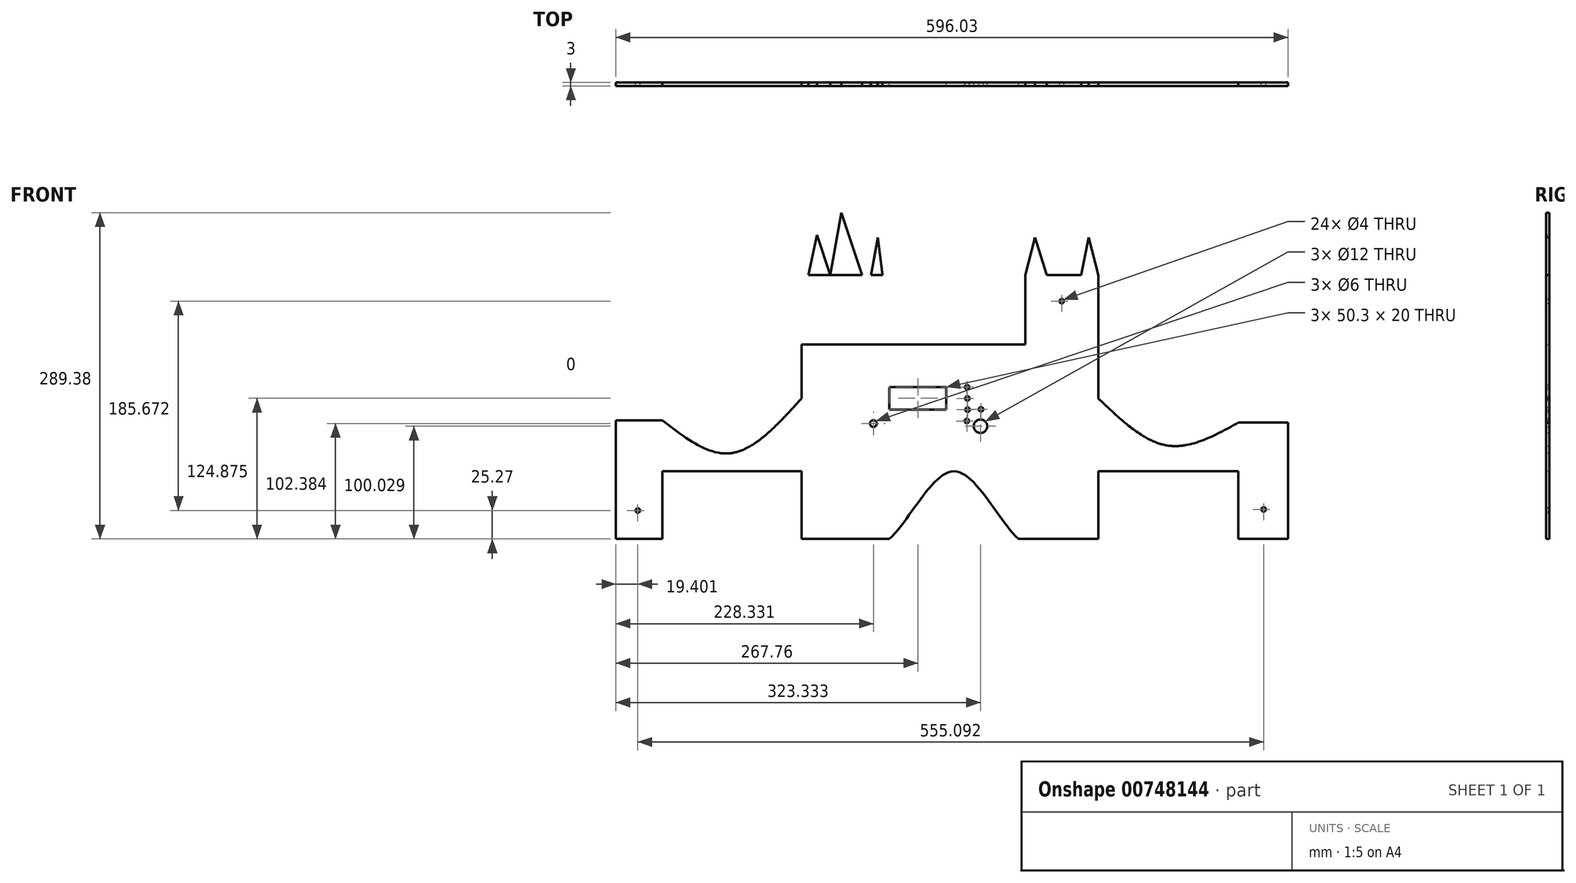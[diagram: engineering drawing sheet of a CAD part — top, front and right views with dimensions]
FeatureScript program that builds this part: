
annotation { "Feature Type Name" : "Feature", "Feature Type Description" : "" }
export const myFeature = defineFeature(function(context is Context, id is Id, definition is map)
    precondition{}
    {
        {
            var Q0;
            Q0=qCreatedBy(makeId("Front.planeOp"),FACE);
            var sketch = newSketch(context, id + "F0", { "sketchPlane" : qUnion([Q0])});
            skLineSegment(sketch, "E0", {"start": v(-242.6, -122.29) * mm, "end": v(-242.6, -42.29) * mm});
            skLineSegment(sketch, "E1", {"start": v(-242.6, -42.29) * mm, "end": v(-201.52, -42.29) * mm});
            skLineSegment(sketch, "E2", {"start": v(-201.52, -42.29) * mm, "end": v(-201.52, -87.66) * mm});
            skLineSegment(sketch, "E3", {"start": v(-201.52, -87.66) * mm, "end": v(-241.16, -87.66) * mm});
            skLineSegment(sketch, "E4", {"start": v(-201.52, -87.66) * mm, "end": v(-78.03, -87.66) * mm});
            skLineSegment(sketch, "E5", {"start": v(-242.6, -122.29) * mm, "end": v(-242.6, -147.66) * mm});
            skLineSegment(sketch, "E6", {"start": v(-242.6, -147.66) * mm, "end": v(-201.52, -147.66) * mm});
            skLineSegment(sketch, "E7", {"start": v(-201.52, -147.66) * mm, "end": v(-201.52, -87.66) * mm});
            skLineSegment(sketch, "E8", {"start": v(-78.03, -87.66) * mm, "end": v(-78.03, -147.66) * mm});
            skLineSegment(sketch, "E9", {"start": v(-78.03, -147.66) * mm, "end": v(0, -147.66) * mm});
            skLineSegment(sketch, "E10", {"start": v(-78.03, -87.66) * mm, "end": v(0, -87.66) * mm});
            skLineSegment(sketch, "E11", {"start": v(0, -87.66) * mm, "end": v(0, -147.66) * mm});
            skLineSegment(sketch, "E12", {"start": v(-78.03, -87.66) * mm, "end": v(-78.03, 24.85) * mm});
            skLineSegment(sketch, "E13", {"start": v(-78.03, 24.85) * mm, "end": v(0, 24.85) * mm});
            skLineSegment(sketch, "E14", {"start": v(0, 24.85) * mm, "end": v(0, -87.66) * mm});
            skLineSegment(sketch, "E15", {"start": v(0, -87.66) * mm, "end": v(114.45, -87.66) * mm});
            skLineSegment(sketch, "E16", {"start": v(117.61, -147.66) * mm, "end": v(185.23, -147.66) * mm});
            skLineSegment(sketch, "E17", {"start": v(185.23, -147.66) * mm, "end": v(185.23, -87.66) * mm});
            skLineSegment(sketch, "E18", {"start": v(185.23, -87.66) * mm, "end": v(114.45, -87.66) * mm});
            skLineSegment(sketch, "E19", {"start": v(114.45, -87.66) * mm, "end": v(114.45, -147.66) * mm});
            skLineSegment(sketch, "E20", {"start": v(114.45, -147.66) * mm, "end": v(117.61, -147.66) * mm});
            skLineSegment(sketch, "E21", {"start": v(114.45, -87.66) * mm, "end": v(114.45, 24.85) * mm});
            skLineSegment(sketch, "E22", {"start": v(185.23, -87.66) * mm, "end": v(185.23, 24.85) * mm});
            skLineSegment(sketch, "E23", {"start": v(185.23, 24.85) * mm, "end": v(114.45, 24.85) * mm});
            skLineSegment(sketch, "E24", {"start": v(-71.9, 24.85) * mm, "end": v(-71.9, 86.5) * mm});
            skLineSegment(sketch, "E25", {"start": v(-6.12, 24.85) * mm, "end": v(-6.12, 86.5) * mm});
            skLineSegment(sketch, "E26", {"start": v(-6.12, 86.5) * mm, "end": v(-6.12, 24.85) * mm});
            skLineSegment(sketch, "E27", {"start": v(-6.12, 86.5) * mm, "end": v(-71.9, 86.5) * mm});
            skLineSegment(sketch, "E28", {"start": v(0, 24.85) * mm, "end": v(114.45, 24.85) * mm});
            skLineSegment(sketch, "E29", {"start": v(0, 13.97) * mm, "end": v(114.45, 13.97) * mm});
            skLineSegment(sketch, "E30", {"start": v(114.45, 13.97) * mm, "end": v(93.44, 24.85) * mm});
            skLineSegment(sketch, "E31", {"start": v(93.44, 24.85) * mm, "end": v(80.38, 13.97) * mm});
            skLineSegment(sketch, "E32", {"start": v(80.38, 13.97) * mm, "end": v(71.32, 24.85) * mm});
            skLineSegment(sketch, "E33", {"start": v(71.32, 24.85) * mm, "end": v(58.25, 13.97) * mm});
            skLineSegment(sketch, "E34", {"start": v(58.25, 13.97) * mm, "end": v(49.19, 24.85) * mm});
            skLineSegment(sketch, "E35", {"start": v(49.19, 24.85) * mm, "end": v(36.12, 13.97) * mm});
            skLineSegment(sketch, "E36", {"start": v(36.12, 13.97) * mm, "end": v(27.06, 24.85) * mm});
            skLineSegment(sketch, "E37", {"start": v(27.06, 24.85) * mm, "end": v(14, 13.97) * mm});
            skLineSegment(sketch, "E38", {"start": v(14, 13.97) * mm, "end": v(0, 24.85) * mm});
            skLineSegment(sketch, "E39", {"start": v(120.47, 24.85) * mm, "end": v(120.47, 86.5) * mm});
            skLineSegment(sketch, "E40", {"start": v(185.23, 24.85) * mm, "end": v(185.23, 86.5) * mm});
            skLineSegment(sketch, "E41", {"start": v(185.23, 86.5) * mm, "end": v(120.47, 86.5) * mm});
            skFitSpline(sketch, "E42", {"points": [v(0, -147.66) * mm, v(57.23, -87.66) * mm, v(114.45, -147.66) * mm], "startDerivative": vector(114.45, 108.74) * mm, "endDerivative": vector(114.45, -108.74) * mm});
            skLineSegment(sketch, "E43", {"start": v(-71.9, 86.5) * mm, "end": v(-64.41, 121.91) * mm});
            skLineSegment(sketch, "E44", {"start": v(-64.41, 121.91) * mm, "end": v(-52.56, 86.5) * mm});
            skLineSegment(sketch, "E45", {"start": v(-52.56, 86.5) * mm, "end": v(-42.84, 141.72) * mm});
            skLineSegment(sketch, "E46", {"start": v(-42.84, 141.72) * mm, "end": v(-24.36, 86.5) * mm});
            skLineSegment(sketch, "E47", {"start": v(-16.37, 86.5) * mm, "end": v(-10.42, 119.89) * mm});
            skLineSegment(sketch, "E48", {"start": v(-10.42, 119.89) * mm, "end": v(-6.12, 86.5) * mm});
            skLineSegment(sketch, "E49", {"start": v(120.47, 86.5) * mm, "end": v(129.04, 119.89) * mm});
            skLineSegment(sketch, "E50", {"start": v(129.04, 119.89) * mm, "end": v(139.65, 86.5) * mm});
            skLineSegment(sketch, "E51", {"start": v(139.65, 86.5) * mm, "end": v(152.85, 86.5) * mm});
            skLineSegment(sketch, "E52", {"start": v(139.65, 86.5) * mm, "end": v(149.07, 132.75) * mm});
            skLineSegment(sketch, "E53", {"start": v(149.07, 132.75) * mm, "end": v(163.78, 86.5) * mm});
            skLineSegment(sketch, "E54", {"start": v(163.78, 86.5) * mm, "end": v(169.95, 86.5) * mm});
            skLineSegment(sketch, "E55", {"start": v(169.95, 86.5) * mm, "end": v(176.75, 119.89) * mm});
            skLineSegment(sketch, "E56", {"start": v(176.75, 119.89) * mm, "end": v(185.23, 86.5) * mm});
            skLineSegment(sketch, "E57", {"start": v(185.23, -87.66) * mm, "end": v(309.46, -87.66) * mm});
            skLineSegment(sketch, "E58", {"start": v(309.46, -87.66) * mm, "end": v(353.42, -87.66) * mm});
            skLineSegment(sketch, "E59", {"start": v(353.42, -87.66) * mm, "end": v(353.42, -147.66) * mm});
            skLineSegment(sketch, "E60", {"start": v(353.42, -147.66) * mm, "end": v(309.46, -147.66) * mm});
            skLineSegment(sketch, "E61", {"start": v(309.46, -147.66) * mm, "end": v(309.46, -87.66) * mm});
            skLineSegment(sketch, "E62", {"start": v(309.46, -87.66) * mm, "end": v(309.46, -44.44) * mm});
            skLineSegment(sketch, "E63", {"start": v(309.46, -44.44) * mm, "end": v(353.42, -44.44) * mm});
            skLineSegment(sketch, "E64", {"start": v(353.42, -44.44) * mm, "end": v(353.42, -87.66) * mm});
            skPoint(sketch, "E65.1.internal.snap0", {"position": v(247.35, -87.66) * mm});
            skFitSpline(sketch, "E65", {"points": [v(309.46, -44.44) * mm, v(247.35, -64.83) * mm, v(185.23, -22.93) * mm], "startDerivative": vector(-130.66, -71.98) * mm, "endDerivative": vector(-117.95, 112.9) * mm});
            skFitSpline(sketch, "E66", {"points": [v(-201.52, -42.29) * mm, v(-141.53, -71.6) * mm, v(-78.03, -22.93) * mm], "startDerivative": vector(126.66, -98.3) * mm, "endDerivative": vector(120.42, 133.53) * mm});
            skPoint(sketch, "E67.2.internal.snap0", {"position": v(-222.06, -42.29) * mm});
            skFitSpline(sketch, "E67", {"points": [v(-201.52, -58.4) * mm, v(-141.53, -81.5) * mm, v(-78.03, -42.29) * mm], "startDerivative": vector(125.17, -77.74) * mm, "endDerivative": vector(121.86, 107.67) * mm});
            skFitSpline(sketch, "E68", {"points": [v(309.46, -58.4) * mm, v(247.35, -78.2) * mm, v(185.23, -42.29) * mm], "startDerivative": vector(-128.74, -67.59) * mm, "endDerivative": vector(-119.8, 98.5) * mm});
            skLineSegment(sketch, "E69", {"start": v(-201.52, -42.29) * mm, "end": v(-191.14, -64.78) * mm});
            skLineSegment(sketch, "E70", {"start": v(-191.14, -64.78) * mm, "end": v(-181.36, -57.93) * mm});
            skLineSegment(sketch, "E71", {"start": v(-181.36, -57.93) * mm, "end": v(-168.22, -76.69) * mm});
            skLineSegment(sketch, "E72", {"start": v(-168.22, -76.69) * mm, "end": v(-159.93, -70.88) * mm});
            skLineSegment(sketch, "E73", {"start": v(-159.93, -70.88) * mm, "end": v(-147.57, -81.64) * mm});
            skLineSegment(sketch, "E74", {"start": v(-147.57, -81.64) * mm, "end": v(-141.53, -71.6) * mm});
            skLineSegment(sketch, "E75", {"start": v(-141.53, -71.6) * mm, "end": v(-129.63, -78.78) * mm});
            skLineSegment(sketch, "E76", {"start": v(-129.63, -78.78) * mm, "end": v(-120.3, -63.3) * mm});
            skLineSegment(sketch, "E77", {"start": v(-120.3, -63.3) * mm, "end": v(-106.51, -71.6) * mm});
            skLineSegment(sketch, "E78", {"start": v(-106.51, -71.6) * mm, "end": v(-106.51, -52.51) * mm});
            skLineSegment(sketch, "E79", {"start": v(-106.51, -52.51) * mm, "end": v(-89.72, -52.51) * mm});
            skLineSegment(sketch, "E80", {"start": v(-89.72, -52.51) * mm, "end": v(-89.72, -35.76) * mm});
            skLineSegment(sketch, "E81", {"start": v(-89.72, -35.76) * mm, "end": v(-78.03, -42.29) * mm});
            skLineSegment(sketch, "E82", {"start": v(309.46, -44.44) * mm, "end": v(297.99, -64.35) * mm});
            skLineSegment(sketch, "E83", {"start": v(297.99, -64.35) * mm, "end": v(288.43, -56.03) * mm});
            skLineSegment(sketch, "E84", {"start": v(288.43, -56.03) * mm, "end": v(276.13, -73.97) * mm});
            skLineSegment(sketch, "E85", {"start": v(276.13, -73.97) * mm, "end": v(262.39, -64.47) * mm});
            skLineSegment(sketch, "E86", {"start": v(262.39, -64.47) * mm, "end": v(255.13, -78.43) * mm});
            skLineSegment(sketch, "E87", {"start": v(255.13, -78.43) * mm, "end": v(247.35, -64.83) * mm});
            skLineSegment(sketch, "E88", {"start": v(234.7, -75.2) * mm, "end": v(247.35, -64.83) * mm});
            skLineSegment(sketch, "E89", {"start": v(234.7, -75.2) * mm, "end": v(224.65, -56.03) * mm});
            skLineSegment(sketch, "E90", {"start": v(224.65, -56.03) * mm, "end": v(214.66, -64.83) * mm});
            skLineSegment(sketch, "E91", {"start": v(214.66, -64.83) * mm, "end": v(214.66, -52.51) * mm});
            skLineSegment(sketch, "E92", {"start": v(214.66, -52.51) * mm, "end": v(205.67, -59.1) * mm});
            skLineSegment(sketch, "E93", {"start": v(205.56, -42.39) * mm, "end": v(205.67, -59.1) * mm});
            skLineSegment(sketch, "E94", {"start": v(205.56, -42.39) * mm, "end": v(192.73, -48.43) * mm});
            skLineSegment(sketch, "E95", {"start": v(192.73, -48.43) * mm, "end": v(192.73, -30.08) * mm});
            skLineSegment(sketch, "E96", {"start": v(185.23, -42.29) * mm, "end": v(192.73, -30.08) * mm});
            skLineSegment(sketch, "E97", {"start": v(-191.14, -64.78) * mm, "end": v(-191.14, -87.66) * mm});
            skLineSegment(sketch, "E98", {"start": v(-160.51, -79.38) * mm, "end": v(-160.51, -87.66) * mm});
            skLineSegment(sketch, "E99", {"start": v(-121.4, -75.2) * mm, "end": v(-121.4, -87.66) * mm});
            skPoint(sketch, "E99.startSnap0", {"position": v(-135.58, -75.2) * mm});
            skLineSegment(sketch, "E100", {"start": v(-89.72, -52.51) * mm, "end": v(-89.72, -87.66) * mm});
            skLineSegment(sketch, "E101", {"start": v(195.6, -50.74) * mm, "end": v(195.6, -87.66) * mm});
            skPoint(sketch, "E101.startSnap0", {"position": v(205.61, -50.74) * mm});
            skLineSegment(sketch, "E102", {"start": v(215.5, -65.67) * mm, "end": v(215.5, -87.66) * mm});
            skLineSegment(sketch, "E103", {"start": v(241.96, -77.32) * mm, "end": v(241.96, -87.66) * mm});
            skLineSegment(sketch, "E104", {"start": v(241.96, -87.66) * mm, "end": v(247.35, -87.66) * mm});
            skLineSegment(sketch, "E105", {"start": v(276.13, -73.97) * mm, "end": v(276.23, -87.66) * mm});
            skLineSegment(sketch, "E106", {"start": v(302.18, -62.21) * mm, "end": v(302.36, -87.66) * mm});
            skSolve(sketch);
        }
        {
            var Q0;
            Q0=qCreatedBy(makeId("Front.planeOp"),FACE);
            var sketch = newSketch(context, id + "F1", { "sketchPlane" : qUnion([Q0])});
            skLineSegment(sketch, "E107.bottom", {"start": v(0, -12.78) * mm, "end": v(50.3, -12.78) * mm});
            skLineSegment(sketch, "E107.top", {"start": v(0, -32.78) * mm, "end": v(50.3, -32.78) * mm});
            skLineSegment(sketch, "E107.left", {"start": v(0, -12.78) * mm, "end": v(0, -32.78) * mm});
            skLineSegment(sketch, "E107.right", {"start": v(50.3, -12.78) * mm, "end": v(50.3, -32.78) * mm});
            skCircle(sketch, "E108", {"center": v(68.87, -12.93) * mm, "radius": 2 * mm});
            skCircle(sketch, "E109", {"center": v(69.14, -22.93) * mm, "radius": 2 * mm});
            skCircle(sketch, "E110", {"center": v(69.23, -32.93) * mm, "radius": 2 * mm});
            skCircle(sketch, "E111", {"center": v(68.6, -42.93) * mm, "radius": 2 * mm});
            skCircle(sketch, "E112", {"center": v(81.23, -32.63) * mm, "radius": 2 * mm});
            skCircle(sketch, "E113", {"center": v(80.72, -47.63) * mm, "radius": 6 * mm});
            skCircle(sketch, "E114", {"center": v(-40.2, 59.04) * mm, "radius": 2 * mm});
            skCircle(sketch, "E115", {"center": v(152.86, 63.28) * mm, "radius": 2 * mm});
            skCircle(sketch, "E116", {"center": v(-223.2, -122.39) * mm, "radius": 2 * mm});
            skCircle(sketch, "E117", {"center": v(331.88, -121.44) * mm, "radius": 2 * mm});
            skCircle(sketch, "E118", {"center": v(-14.28, -45.28) * mm, "radius": 3 * mm});
            skSolve(sketch);
        }
        {
            var Q0;
            Q0=makeQuery(id+"F1.imprint","IMPRINT",FACE,{"disambiguationData":[TD([[makeQuery(id+"F1.imprint","IMPRINT",EDGE,{"derivedFrom":sQuery(id+"F1.wireOp",EDGE,"E107.bottom")}),-1.0]])]});
            var Q1;
            {var subQ3=sQuery(id+"F0.wireOp",EDGE,"E106");Q1=makeQuery(id+"F0.imprint","IMPRINT",FACE,{"disambiguationData":[TD([[makeQuery(id+"F0.imprint","IMPRINT",EDGE,{"derivedFrom":subQ3}),1.0]])]});}
            var Q2;
            {var subQ2=sQuery(id+"F0.wireOp",EDGE,"E105");Q2=makeQuery(id+"F0.imprint","IMPRINT",FACE,{"disambiguationData":[TD([[makeQuery(id+"F0.imprint","IMPRINT",EDGE,{"derivedFrom":subQ2}),1.0]])]});}
            var Q3;
            {var subQ3=sQuery(id+"F0.wireOp",EDGE,"E103");Q3=makeQuery(id+"F0.imprint","IMPRINT",FACE,{"disambiguationData":[TD([[makeQuery(id+"F0.imprint","IMPRINT",EDGE,{"derivedFrom":subQ3}),1.0]])]});}
            var Q4;
            {var subQ4=sQuery(id+"F0.wireOp",EDGE,"E98");Q4=makeQuery(id+"F0.imprint","IMPRINT",FACE,{"disambiguationData":[TD([[makeQuery(id+"F0.imprint","IMPRINT",EDGE,{"derivedFrom":subQ4}),1.0]])]});}
            var Q5;
            {var subQ0=sQuery(id+"F0.wireOp",EDGE,"E69");Q5=makeQuery(id+"F0.imprint","IMPRINT",FACE,{"disambiguationData":[TD([[makeQuery(id+"F0.imprint","IMPRINT",EDGE,{"derivedFrom":subQ0}),1.0]])]});}
            var Q6;
            {var subQ0=sQuery(id+"F0.wireOp",EDGE,"E79");Q6=makeQuery(id+"F0.imprint","IMPRINT",FACE,{"disambiguationData":[TD([[makeQuery(id+"F0.imprint","IMPRINT",EDGE,{"derivedFrom":subQ0}),1.0]])]});}
            var Q7;
            {var subQ0=sQuery(id+"F0.wireOp",EDGE,"E77");var subQ5=sQuery(id+"F0.wireOp",EDGE,"E67");var subQ6=makeQuery(id+"F0.imprint","INTERSECT",VERTEX,{"derivedFrom":[subQ5,subQ0]});Q7=makeQuery(id+"F0.imprint","IMPRINT",FACE,{"disambiguationData":[TD([[makeQuery(id+"F0.imprint","IMPRINT",EDGE,{"disambiguationData":[TD([[subQ6,-1.0]])],"derivedFrom":subQ5}),1.0]])]});}
            var Q8;
            {var subQ0=sQuery(id+"F0.wireOp",EDGE,"E76");Q8=makeQuery(id+"F0.imprint","IMPRINT",FACE,{"disambiguationData":[TD([[makeQuery(id+"F0.imprint","IMPRINT",EDGE,{"derivedFrom":subQ0}),-1.0]])]});}
            var Q9;
            {var subQ0=sQuery(id+"F0.wireOp",EDGE,"E79");Q9=makeQuery(id+"F0.imprint","IMPRINT",FACE,{"disambiguationData":[TD([[makeQuery(id+"F0.imprint","IMPRINT",EDGE,{"derivedFrom":subQ0}),-1.0]])]});}
            var Q10;
            {var subQ7=sQuery(id+"F0.wireOp",EDGE,"E99");Q10=makeQuery(id+"F0.imprint","IMPRINT",FACE,{"disambiguationData":[TD([[makeQuery(id+"F0.imprint","IMPRINT",EDGE,{"derivedFrom":subQ7}),1.0]])]});}
            var Q11;
            {var subQ0=sQuery(id+"F0.wireOp",EDGE,"E91");Q11=makeQuery(id+"F0.imprint","IMPRINT",FACE,{"disambiguationData":[TD([[makeQuery(id+"F0.imprint","IMPRINT",EDGE,{"derivedFrom":subQ0}),1.0]])]});}
            var Q12;
            {var subQ0=sQuery(id+"F0.wireOp",EDGE,"E89");Q12=makeQuery(id+"F0.imprint","IMPRINT",FACE,{"disambiguationData":[TD([[makeQuery(id+"F0.imprint","IMPRINT",EDGE,{"derivedFrom":subQ0}),1.0]])]});}
            var Q13;
            {var subQ1=sQuery(id+"F0.wireOp",EDGE,"E90");Q13=makeQuery(id+"F0.imprint","IMPRINT",FACE,{"disambiguationData":[TD([[makeQuery(id+"F0.imprint","IMPRINT",EDGE,{"derivedFrom":subQ1}),-1.0]])]});}
            var Q14;
            {var subQ0=sQuery(id+"F0.wireOp",EDGE,"E88");Q14=makeQuery(id+"F0.imprint","IMPRINT",FACE,{"disambiguationData":[TD([[makeQuery(id+"F0.imprint","IMPRINT",EDGE,{"derivedFrom":subQ0}),1.0]])]});}
            var Q15;
            {var subQ3=sQuery(id+"F0.wireOp",EDGE,"E30");Q15=makeQuery(id+"F0.imprint","IMPRINT",FACE,{"disambiguationData":[TD([[makeQuery(id+"F0.imprint","IMPRINT",EDGE,{"derivedFrom":subQ3}),-1.0]])]});}
            var Q16;
            {var subQ0=sQuery(id+"F0.wireOp",EDGE,"E33");Q16=makeQuery(id+"F0.imprint","IMPRINT",FACE,{"disambiguationData":[TD([[makeQuery(id+"F0.imprint","IMPRINT",EDGE,{"derivedFrom":subQ0}),-1.0]])]});}
            var Q17;
            {var subQ3=sQuery(id+"F0.wireOp",EDGE,"E29");var subQ7=sQuery(id+"F0.wireOp",EDGE,"E14");var subQ9=makeQuery(id+"F0.imprint","INTERSECT",VERTEX,{"derivedFrom":[subQ7,subQ3]});Q17=makeQuery(id+"F0.imprint","IMPRINT",FACE,{"disambiguationData":[TD([[makeQuery(id+"F0.imprint","IMPRINT",EDGE,{"disambiguationData":[TD([[subQ9,-1.0]])],"derivedFrom":subQ3}),-1.0]])]});}
            var Q18;
            {var subQ0=sQuery(id+"F0.wireOp",EDGE,"E36");Q18=makeQuery(id+"F0.imprint","IMPRINT",FACE,{"disambiguationData":[TD([[makeQuery(id+"F0.imprint","IMPRINT",EDGE,{"derivedFrom":subQ0}),1.0]])]});}
            var Q19;
            {var subQ0=sQuery(id+"F0.wireOp",EDGE,"E35");Q19=makeQuery(id+"F0.imprint","IMPRINT",FACE,{"disambiguationData":[TD([[makeQuery(id+"F0.imprint","IMPRINT",EDGE,{"derivedFrom":subQ0}),-1.0]])]});}
            var Q20;
            {var subQ10=sQuery(id+"F0.wireOp",EDGE,"E101");Q20=makeQuery(id+"F0.imprint","IMPRINT",FACE,{"disambiguationData":[TD([[makeQuery(id+"F0.imprint","IMPRINT",EDGE,{"derivedFrom":subQ10}),1.0]])]});}
            var Q21;
            {var subQ0=sQuery(id+"F0.wireOp",EDGE,"E19");Q21=makeQuery(id+"F0.imprint","IMPRINT",FACE,{"disambiguationData":[TD([[makeQuery(id+"F0.imprint","IMPRINT",EDGE,{"derivedFrom":subQ0}),-1.0]])]});}
            var Q22;
            {var subQ0=sQuery(id+"F0.wireOp",EDGE,"E34");Q22=makeQuery(id+"F0.imprint","IMPRINT",FACE,{"disambiguationData":[TD([[makeQuery(id+"F0.imprint","IMPRINT",EDGE,{"derivedFrom":subQ0}),1.0]])]});}
            var Q23;
            {var subQ3=sQuery(id+"F0.wireOp",EDGE,"E81");Q23=makeQuery(id+"F0.imprint","IMPRINT",FACE,{"disambiguationData":[TD([[makeQuery(id+"F0.imprint","IMPRINT",EDGE,{"derivedFrom":subQ3}),1.0]])]});}
            var Q24;
            {var subQ0=sQuery(id+"F0.wireOp",EDGE,"E87");Q24=makeQuery(id+"F0.imprint","IMPRINT",FACE,{"disambiguationData":[TD([[makeQuery(id+"F0.imprint","IMPRINT",EDGE,{"derivedFrom":subQ0}),1.0]])]});}
            var Q25;
            {var subQ2=sQuery(id+"F0.wireOp",EDGE,"E37");Q25=makeQuery(id+"F0.imprint","IMPRINT",FACE,{"disambiguationData":[TD([[makeQuery(id+"F0.imprint","IMPRINT",EDGE,{"derivedFrom":subQ2}),-1.0]])]});}
            var Q26;
            {var subQ4=sQuery(id+"F0.wireOp",EDGE,"E18");Q26=makeQuery(id+"F0.imprint","IMPRINT",FACE,{"disambiguationData":[TD([[makeQuery(id+"F0.imprint","IMPRINT",EDGE,{"derivedFrom":subQ4}),-1.0]])]});}
            var Q27;
            {var subQ5=sQuery(id+"F0.wireOp",EDGE,"E10");Q27=makeQuery(id+"F0.imprint","IMPRINT",FACE,{"disambiguationData":[TD([[makeQuery(id+"F0.imprint","IMPRINT",EDGE,{"derivedFrom":subQ5}),1.0]])]});}
            var Q28;
            {var subQ3=sQuery(id+"F0.wireOp",EDGE,"E96");Q28=makeQuery(id+"F0.imprint","IMPRINT",FACE,{"disambiguationData":[TD([[makeQuery(id+"F0.imprint","IMPRINT",EDGE,{"derivedFrom":subQ3}),1.0]])]});}
            var Q29;
            {var subQ0=sQuery(id+"F0.wireOp",EDGE,"E31");Q29=makeQuery(id+"F0.imprint","IMPRINT",FACE,{"disambiguationData":[TD([[makeQuery(id+"F0.imprint","IMPRINT",EDGE,{"derivedFrom":subQ0}),-1.0]])]});}
            var Q30;
            {var subQ0=sQuery(id+"F0.wireOp",EDGE,"E38");Q30=makeQuery(id+"F0.imprint","IMPRINT",FACE,{"disambiguationData":[TD([[makeQuery(id+"F0.imprint","IMPRINT",EDGE,{"derivedFrom":subQ0}),1.0]])]});}
            var Q31;
            Q31=makeQuery(id+"F0.imprint","IMPRINT",FACE,{"disambiguationData":[TD([[makeQuery(id+"F0.imprint","IMPRINT",EDGE,{"derivedFrom":sQuery(id+"F0.wireOp",EDGE,"E8")}),1.0]])]});
            var Q32;
            {var subQ3=sQuery(id+"F0.wireOp",EDGE,"E100");Q32=makeQuery(id+"F0.imprint","IMPRINT",FACE,{"disambiguationData":[TD([[makeQuery(id+"F0.imprint","IMPRINT",EDGE,{"derivedFrom":subQ3}),1.0]])]});}
            var Q33;
            Q33=makeQuery(id+"F0.imprint","IMPRINT",FACE,{"disambiguationData":[TD([[makeQuery(id+"F0.imprint","IMPRINT",EDGE,{"derivedFrom":sQuery(id+"F0.wireOp",EDGE,"E0")}),-1.0]])]});
            var Q34;
            {var subQ0=sQuery(id+"F0.wireOp",EDGE,"E82");Q34=makeQuery(id+"F0.imprint","IMPRINT",FACE,{"disambiguationData":[TD([[makeQuery(id+"F0.imprint","IMPRINT",EDGE,{"derivedFrom":subQ0}),1.0]])]});}
            var Q35;
            {var subQ5=sQuery(id+"F0.wireOp",EDGE,"E97");Q35=makeQuery(id+"F0.imprint","IMPRINT",FACE,{"disambiguationData":[TD([[makeQuery(id+"F0.imprint","IMPRINT",EDGE,{"derivedFrom":subQ5}),-1.0]])]});}
            var Q36;
            {var subQ0=sQuery(id+"F0.wireOp",EDGE,"E69");Q36=makeQuery(id+"F0.imprint","IMPRINT",FACE,{"disambiguationData":[TD([[makeQuery(id+"F0.imprint","IMPRINT",EDGE,{"derivedFrom":subQ0}),-1.0]])]});}
            var Q37;
            {var subQ2=sQuery(id+"F0.wireOp",EDGE,"E47");Q37=makeQuery(id+"F0.imprint","IMPRINT",FACE,{"disambiguationData":[TD([[makeQuery(id+"F0.imprint","IMPRINT",EDGE,{"derivedFrom":subQ2}),-1.0]])]});}
            var Q38;
            {var subQ0=sQuery(id+"F0.wireOp",EDGE,"E70");Q38=makeQuery(id+"F0.imprint","IMPRINT",FACE,{"disambiguationData":[TD([[makeQuery(id+"F0.imprint","IMPRINT",EDGE,{"derivedFrom":subQ0}),-1.0]])]});}
            var Q39;
            {var subQ0=sQuery(id+"F0.wireOp",EDGE,"E51");Q39=makeQuery(id+"F0.imprint","IMPRINT",FACE,{"disambiguationData":[TD([[makeQuery(id+"F0.imprint","IMPRINT",EDGE,{"derivedFrom":subQ0}),1.0]])]});}
            var Q40;
            {var subQ3=sQuery(id+"F0.wireOp",EDGE,"E39");Q40=makeQuery(id+"F0.imprint","IMPRINT",FACE,{"disambiguationData":[TD([[makeQuery(id+"F0.imprint","IMPRINT",EDGE,{"derivedFrom":subQ3}),-1.0]])]});}
            var Q41;
            {var subQ0=sQuery(id+"F0.wireOp",EDGE,"E97");Q41=makeQuery(id+"F0.imprint","IMPRINT",FACE,{"disambiguationData":[TD([[makeQuery(id+"F0.imprint","IMPRINT",EDGE,{"derivedFrom":subQ0}),1.0]])]});}
            var Q42;
            {var subQ0=sQuery(id+"F0.wireOp",EDGE,"E45");Q42=makeQuery(id+"F0.imprint","IMPRINT",FACE,{"disambiguationData":[TD([[makeQuery(id+"F0.imprint","IMPRINT",EDGE,{"derivedFrom":subQ0}),-1.0]])]});}
            var Q43;
            {var subQ0=sQuery(id+"F0.wireOp",EDGE,"E32");Q43=makeQuery(id+"F0.imprint","IMPRINT",FACE,{"disambiguationData":[TD([[makeQuery(id+"F0.imprint","IMPRINT",EDGE,{"derivedFrom":subQ0}),1.0]])]});}
            var Q44;
            {var subQ0=sQuery(id+"F0.wireOp",EDGE,"E30");Q44=makeQuery(id+"F0.imprint","IMPRINT",FACE,{"disambiguationData":[TD([[makeQuery(id+"F0.imprint","IMPRINT",EDGE,{"derivedFrom":subQ0}),1.0]])]});}
            var Q45;
            Q45=makeQuery(id+"F0.imprint","IMPRINT",FACE,{"disambiguationData":[TD([[makeQuery(id+"F0.imprint","IMPRINT",EDGE,{"derivedFrom":sQuery(id+"F0.wireOp",EDGE,"E58")}),-1.0]])]});
            var Q46;
            {var subQ0=sQuery(id+"F0.wireOp",EDGE,"E11");Q46=makeQuery(id+"F0.imprint","IMPRINT",FACE,{"disambiguationData":[TD([[makeQuery(id+"F0.imprint","IMPRINT",EDGE,{"derivedFrom":subQ0}),1.0]])]});}
            var Q47;
            {var subQ6=sQuery(id+"F0.wireOp",EDGE,"E101");Q47=makeQuery(id+"F0.imprint","IMPRINT",FACE,{"disambiguationData":[TD([[makeQuery(id+"F0.imprint","IMPRINT",EDGE,{"derivedFrom":subQ6}),-1.0]])]});}
            var Q48;
            {var subQ2=sQuery(id+"F0.wireOp",EDGE,"E55");Q48=makeQuery(id+"F0.imprint","IMPRINT",FACE,{"disambiguationData":[TD([[makeQuery(id+"F0.imprint","IMPRINT",EDGE,{"derivedFrom":subQ2}),-1.0]])]});}
            var Q49;
            Q49=makeQuery(id+"F0.imprint","IMPRINT",FACE,{"disambiguationData":[TD([[makeQuery(id+"F0.imprint","IMPRINT",EDGE,{"derivedFrom":sQuery(id+"F0.wireOp",EDGE,"E16")}),1.0]])]});
            var Q50;
            {var subQ1=sQuery(id+"F0.wireOp",EDGE,"E26");Q50=makeQuery(id+"F0.imprint","IMPRINT",FACE,{"disambiguationData":[TD([[makeQuery(id+"F0.imprint","IMPRINT",EDGE,{"derivedFrom":subQ1}),-1.0]])]});}
            var Q51;
            {var subQ0=sQuery(id+"F0.wireOp",EDGE,"E43");Q51=makeQuery(id+"F0.imprint","IMPRINT",FACE,{"disambiguationData":[TD([[makeQuery(id+"F0.imprint","IMPRINT",EDGE,{"derivedFrom":subQ0}),-1.0]])]});}
            var Q52;
            {var subQ0=sQuery(id+"F0.wireOp",EDGE,"E49");Q52=makeQuery(id+"F0.imprint","IMPRINT",FACE,{"disambiguationData":[TD([[makeQuery(id+"F0.imprint","IMPRINT",EDGE,{"derivedFrom":subQ0}),-1.0]])]});}
            var Q53;
            {var subQ2=sQuery(id+"F0.wireOp",EDGE,"E58");Q53=makeQuery(id+"F0.imprint","IMPRINT",FACE,{"disambiguationData":[TD([[makeQuery(id+"F0.imprint","IMPRINT",EDGE,{"derivedFrom":subQ2}),1.0]])]});}
            var Q54;
            {var subQ2=sQuery(id+"F0.wireOp",EDGE,"E80");Q54=makeQuery(id+"F0.imprint","IMPRINT",FACE,{"disambiguationData":[TD([[makeQuery(id+"F0.imprint","IMPRINT",EDGE,{"derivedFrom":subQ2}),-1.0]])]});}
            var Q55;
            {var subQ0=sQuery(id+"F0.wireOp",EDGE,"E82");Q55=makeQuery(id+"F0.imprint","IMPRINT",FACE,{"disambiguationData":[TD([[makeQuery(id+"F0.imprint","IMPRINT",EDGE,{"derivedFrom":subQ0}),-1.0]])]});}
            var Q56;
            {var subQ0=sQuery(id+"F0.wireOp",EDGE,"E83");Q56=makeQuery(id+"F0.imprint","IMPRINT",FACE,{"disambiguationData":[TD([[makeQuery(id+"F0.imprint","IMPRINT",EDGE,{"derivedFrom":subQ0}),1.0]])]});}
            var Q57;
            {var subQ0=sQuery(id+"F0.wireOp",EDGE,"E86");Q57=makeQuery(id+"F0.imprint","IMPRINT",FACE,{"disambiguationData":[TD([[makeQuery(id+"F0.imprint","IMPRINT",EDGE,{"derivedFrom":subQ0}),-1.0]])]});}
            var Q58;
            {var subQ0=sQuery(id+"F0.wireOp",EDGE,"E85");Q58=makeQuery(id+"F0.imprint","IMPRINT",FACE,{"disambiguationData":[TD([[makeQuery(id+"F0.imprint","IMPRINT",EDGE,{"derivedFrom":subQ0}),1.0]])]});}
            var Q59;
            Q59=makeQuery(id+"F1.imprint","IMPRINT",FACE,{"disambiguationData":[TD([[makeQuery(id+"F1.imprint","IMPRINT",EDGE,{"derivedFrom":sQuery(id+"F1.wireOp",EDGE,"E118")}),1.0]])]});
            var Q60;
            Q60=makeQuery(id+"F1.imprint","IMPRINT",FACE,{"disambiguationData":[TD([[makeQuery(id+"F1.imprint","IMPRINT",EDGE,{"derivedFrom":sQuery(id+"F1.wireOp",EDGE,"E113")}),1.0]])]});
            var Q61;
            {var subQ0=sQuery(id+"F0.wireOp",EDGE,"E77");var subQ1=sQuery(id+"F0.wireOp",EDGE,"E67");var subQ2=makeQuery(id+"F0.imprint","INTERSECT",VERTEX,{"derivedFrom":[subQ1,subQ0]});Q61=makeQuery(id+"F0.imprint","IMPRINT",FACE,{"disambiguationData":[TD([[makeQuery(id+"F0.imprint","IMPRINT",EDGE,{"disambiguationData":[TD([[subQ2,-1.0]])],"derivedFrom":subQ1}),-1.0]])]});}
            var Q62;
            {var subQ0=sQuery(id+"F0.wireOp",EDGE,"E72");Q62=makeQuery(id+"F0.imprint","IMPRINT",FACE,{"disambiguationData":[TD([[makeQuery(id+"F0.imprint","IMPRINT",EDGE,{"derivedFrom":subQ0}),-1.0]])]});}
            var Q63;
            {var subQ4=sQuery(id+"F0.wireOp",EDGE,"E94");Q63=makeQuery(id+"F0.imprint","IMPRINT",FACE,{"disambiguationData":[TD([[makeQuery(id+"F0.imprint","IMPRINT",EDGE,{"derivedFrom":subQ4}),1.0]])]});}
            var Q64;
            {var subQ2=sQuery(id+"F0.wireOp",EDGE,"E95");Q64=makeQuery(id+"F0.imprint","IMPRINT",FACE,{"disambiguationData":[TD([[makeQuery(id+"F0.imprint","IMPRINT",EDGE,{"derivedFrom":subQ2}),1.0]])]});}
            var Q65;
            {var subQ0=sQuery(id+"F0.wireOp",EDGE,"E74");Q65=makeQuery(id+"F0.imprint","IMPRINT",FACE,{"disambiguationData":[TD([[makeQuery(id+"F0.imprint","IMPRINT",EDGE,{"derivedFrom":subQ0}),-1.0]])]});}
            var Q66;
            {var subQ0=sQuery(id+"F0.wireOp",EDGE,"E75");Q66=makeQuery(id+"F0.imprint","IMPRINT",FACE,{"disambiguationData":[TD([[makeQuery(id+"F0.imprint","IMPRINT",EDGE,{"derivedFrom":subQ0}),1.0]])]});}
            var Q67;
            Q67=makeQuery(id+"F1.imprint","IMPRINT",FACE,{"disambiguationData":[TD([[makeQuery(id+"F1.imprint","IMPRINT",EDGE,{"derivedFrom":sQuery(id+"F1.wireOp",EDGE,"E116")}),1.0]])]});
            var Q68;
            Q68=makeQuery(id+"F1.imprint","IMPRINT",FACE,{"disambiguationData":[TD([[makeQuery(id+"F1.imprint","IMPRINT",EDGE,{"derivedFrom":sQuery(id+"F1.wireOp",EDGE,"E111")}),1.0]])]});
            var Q69;
            Q69=makeQuery(id+"F1.imprint","IMPRINT",FACE,{"disambiguationData":[TD([[makeQuery(id+"F1.imprint","IMPRINT",EDGE,{"derivedFrom":sQuery(id+"F1.wireOp",EDGE,"E114")}),1.0]])]});
            var Q70;
            Q70=makeQuery(id+"F1.imprint","IMPRINT",FACE,{"disambiguationData":[TD([[makeQuery(id+"F1.imprint","IMPRINT",EDGE,{"derivedFrom":sQuery(id+"F1.wireOp",EDGE,"E110")}),1.0]])]});
            var Q71;
            Q71=makeQuery(id+"F1.imprint","IMPRINT",FACE,{"disambiguationData":[TD([[makeQuery(id+"F1.imprint","IMPRINT",EDGE,{"derivedFrom":sQuery(id+"F1.wireOp",EDGE,"E109")}),1.0]])]});
            var Q72;
            Q72=makeQuery(id+"F1.imprint","IMPRINT",FACE,{"disambiguationData":[TD([[makeQuery(id+"F1.imprint","IMPRINT",EDGE,{"derivedFrom":sQuery(id+"F1.wireOp",EDGE,"E112")}),1.0]])]});
            var Q73;
            Q73=makeQuery(id+"F1.imprint","IMPRINT",FACE,{"disambiguationData":[TD([[makeQuery(id+"F1.imprint","IMPRINT",EDGE,{"derivedFrom":sQuery(id+"F1.wireOp",EDGE,"E115")}),1.0]])]});
            var Q74;
            Q74=makeQuery(id+"F1.imprint","IMPRINT",FACE,{"disambiguationData":[TD([[makeQuery(id+"F1.imprint","IMPRINT",EDGE,{"derivedFrom":sQuery(id+"F1.wireOp",EDGE,"E108")}),1.0]])]});
            var Q75;
            Q75=makeQuery(id+"F1.imprint","IMPRINT",FACE,{"disambiguationData":[TD([[makeQuery(id+"F1.imprint","IMPRINT",EDGE,{"derivedFrom":sQuery(id+"F1.wireOp",EDGE,"E117")}),1.0]])]});
            var Q76;
            {var subQ0=sQuery(id+"F0.wireOp",EDGE,"E92");var subQ1=sQuery(id+"F0.wireOp",EDGE,"E68");var subQ2=makeQuery(id+"F0.imprint","INTERSECT",VERTEX,{"derivedFrom":[subQ1,subQ0]});Q76=makeQuery(id+"F0.imprint","IMPRINT",FACE,{"disambiguationData":[TD([[makeQuery(id+"F0.imprint","IMPRINT",EDGE,{"disambiguationData":[TD([[subQ2,-1.0]])],"derivedFrom":subQ1}),1.0]])]});}
            extrude(context, id + "F2", {"entities" : qUnion([Q0, Q1, Q2, Q3, Q4, Q5, Q6, Q7, Q8, Q9, Q10, Q11, Q12, Q13, Q14, Q15, Q16, Q17, Q18, Q19, Q20, Q21, Q22, Q23, Q24, Q25, Q26, Q27, Q28, Q29, Q30, Q31, Q32, Q33, Q34, Q35, Q36, Q37, Q38, Q39, Q40, Q41, Q42, Q43, Q44, Q45, Q46, Q47, Q48, Q49, Q50, Q51, Q52, Q53, Q54, Q55, Q56, Q57, Q58, Q59, Q60, Q61, Q62, Q63, Q64, Q65, Q66, Q67, Q68, Q69, Q70, Q71, Q72, Q73, Q74, Q75, Q76]), "depth" : 3 * mm, "offsetDistance" : 25 * mm});
        }
        {
            var Q0;
            Q0 = qSketchRegion(id + "F1", true);
            extrude(context, id + "F3", {"entities" : qUnion([Q0]), "operationType" : NewBodyOperationType.REMOVE, "depth" : 54 * mm, "offsetDistance" : 25 * mm});
        }
        {
            var Q0;
            Q0=makeQuery(id+"F2.opExtrude","CAP_FACE",FACE,{"disambiguationData":[OSD([sQuery(id+"F0.wireOp",EDGE,"E0"),sQuery(id+"F0.wireOp",EDGE,"E1"),sQuery(id+"F0.wireOp",EDGE,"E4"),sQuery(id+"F0.wireOp",EDGE,"E5"),sQuery(id+"F0.wireOp",EDGE,"E6"),sQuery(id+"F0.wireOp",EDGE,"E7"),sQuery(id+"F0.wireOp",EDGE,"E8"),sQuery(id+"F0.wireOp",EDGE,"E9"),sQuery(id+"F0.wireOp",EDGE,"E12"),sQuery(id+"F0.wireOp",EDGE,"E13"),sQuery(id+"F0.wireOp",EDGE,"E16"),sQuery(id+"F0.wireOp",EDGE,"E17"),sQuery(id+"F0.wireOp",EDGE,"E20"),sQuery(id+"F0.wireOp",EDGE,"E22"),sQuery(id+"F0.wireOp",EDGE,"E23"),sQuery(id+"F0.wireOp",EDGE,"E26"),sQuery(id+"F0.wireOp",EDGE,"E24"),sQuery(id+"F0.wireOp",EDGE,"E27"),sQuery(id+"F0.wireOp",EDGE,"E28"),sQuery(id+"F0.wireOp",EDGE,"E39"),sQuery(id+"F0.wireOp",EDGE,"E40"),sQuery(id+"F0.wireOp",EDGE,"E42"),sQuery(id+"F0.wireOp",EDGE,"E43"),sQuery(id+"F0.wireOp",EDGE,"E44"),sQuery(id+"F0.wireOp",EDGE,"E45"),sQuery(id+"F0.wireOp",EDGE,"E46"),sQuery(id+"F0.wireOp",EDGE,"E47"),sQuery(id+"F0.wireOp",EDGE,"E48"),sQuery(id+"F0.wireOp",EDGE,"E49"),sQuery(id+"F0.wireOp",EDGE,"E50"),sQuery(id+"F0.wireOp",EDGE,"E52"),sQuery(id+"F0.wireOp",EDGE,"E53"),sQuery(id+"F0.wireOp",EDGE,"E54"),sQuery(id+"F0.wireOp",EDGE,"E55"),sQuery(id+"F0.wireOp",EDGE,"E56"),sQuery(id+"F0.wireOp",EDGE,"E57"),sQuery(id+"F0.wireOp",EDGE,"E59"),sQuery(id+"F0.wireOp",EDGE,"E60"),sQuery(id+"F0.wireOp",EDGE,"E61"),sQuery(id+"F0.wireOp",EDGE,"E63"),sQuery(id+"F0.wireOp",EDGE,"E64"),sQuery(id+"F0.wireOp",EDGE,"E65"),sQuery(id+"F0.wireOp",EDGE,"E66"),sQuery(id+"F0.wireOp",EDGE,"E104")])],"isStart":true});
            var Q1;
            Q1=makeQuery(id+"F2.opExtrude","SWEPT_FACE",FACE,{"disambiguationData":[OSD([sQuery(id+"F1.wireOp",EDGE,"E107.top")])]});
            var Q2;
            Q2=makeQuery(id+"F2.opExtrude","SWEPT_FACE",FACE,{"disambiguationData":[OSD([sQuery(id+"F1.wireOp",EDGE,"E107.bottom")])]});
            var Q3;
            Q3=makeQuery(id+"F2.opExtrude","SWEPT_FACE",FACE,{"disambiguationData":[OSD([sQuery(id+"F1.wireOp",EDGE,"E107.right")])]});
            var Q4;
            Q4=makeQuery(id+"F2.opExtrude","CAP_FACE",FACE,{"disambiguationData":[OSD([sQuery(id+"F1.wireOp",EDGE,"E107.bottom"),sQuery(id+"F1.wireOp",EDGE,"E107.top"),sQuery(id+"F1.wireOp",EDGE,"E107.left"),sQuery(id+"F1.wireOp",EDGE,"E107.right")])],"isStart":false});
            var Q5;
            Q5=makeQuery(id+"F2.opExtrude","CAP_FACE",FACE,{"disambiguationData":[OSD([sQuery(id+"F1.wireOp",EDGE,"E112")])],"isStart":false});
            var Q6;
            Q6=makeQuery(id+"F2.opExtrude","CAP_FACE",FACE,{"disambiguationData":[OSD([sQuery(id+"F1.wireOp",EDGE,"E109")])],"isStart":false});
            var Q7;
            Q7=makeQuery(id+"F2.opExtrude","CAP_FACE",FACE,{"disambiguationData":[OSD([sQuery(id+"F1.wireOp",EDGE,"E110")])],"isStart":false});
            var Q8;
            Q8=makeQuery(id+"F2.opExtrude","CAP_FACE",FACE,{"disambiguationData":[OSD([sQuery(id+"F1.wireOp",EDGE,"E111")])],"isStart":false});
            var Q9;
            Q9=makeQuery(id+"F2.opExtrude","CAP_FACE",FACE,{"disambiguationData":[OSD([sQuery(id+"F1.wireOp",EDGE,"E108")])],"isStart":false});
            var Q10;
            Q10=makeQuery(id+"F2.opExtrude","CAP_FACE",FACE,{"disambiguationData":[OSD([sQuery(id+"F1.wireOp",EDGE,"E118")])],"isStart":false});
            var Q11;
            Q11=makeQuery(id+"F2.opExtrude","CAP_FACE",FACE,{"disambiguationData":[OSD([sQuery(id+"F1.wireOp",EDGE,"E107.bottom"),sQuery(id+"F1.wireOp",EDGE,"E107.top"),sQuery(id+"F1.wireOp",EDGE,"E107.left"),sQuery(id+"F1.wireOp",EDGE,"E107.right")])],"isStart":true});
            var Q12;
            Q12=makeQuery(id+"F2.opExtrude","SWEPT_FACE",FACE,{"disambiguationData":[OSD([sQuery(id+"F1.wireOp",EDGE,"E107.left")])]});
            var Q13;
            Q13=makeQuery(id+"F2.opExtrude","CAP_FACE",FACE,{"disambiguationData":[OSD([sQuery(id+"F1.wireOp",EDGE,"E112")])],"isStart":true});
            var Q14;
            Q14=makeQuery(id+"F2.opExtrude","CAP_FACE",FACE,{"disambiguationData":[OSD([sQuery(id+"F1.wireOp",EDGE,"E109")])],"isStart":true});
            var Q15;
            Q15=makeQuery(id+"F2.opExtrude","CAP_FACE",FACE,{"disambiguationData":[OSD([sQuery(id+"F1.wireOp",EDGE,"E110")])],"isStart":true});
            var Q16;
            Q16=makeQuery(id+"F2.opExtrude","CAP_FACE",FACE,{"disambiguationData":[OSD([sQuery(id+"F1.wireOp",EDGE,"E111")])],"isStart":true});
            var Q17;
            Q17=makeQuery(id+"F2.opExtrude","CAP_FACE",FACE,{"disambiguationData":[OSD([sQuery(id+"F1.wireOp",EDGE,"E108")])],"isStart":true});
            var Q18;
            Q18=makeQuery(id+"F2.opExtrude","CAP_FACE",FACE,{"disambiguationData":[OSD([sQuery(id+"F1.wireOp",EDGE,"E118")])],"isStart":true});
            extrude(context, id + "F4", {"entities" : qUnion([Q0, Q1, Q2, Q3, Q4, Q5, Q6, Q7, Q8, Q9, Q10, Q11, Q12, Q13, Q14, Q15, Q16, Q17, Q18]), "oppositeDirection" : true, "depth" : 3 * mm, "offsetDistance" : 25 * mm});
        }
        {
            var Q0;
            Q0=makeQuery(id+"F2.opExtrude","CAP_FACE",FACE,{"disambiguationData":[OSD([sQuery(id+"F1.wireOp",EDGE,"E115")])],"isStart":false});
            var Q1;
            Q1=makeQuery(id+"F2.opExtrude","CAP_FACE",FACE,{"disambiguationData":[OSD([sQuery(id+"F1.wireOp",EDGE,"E115")])],"isStart":true});
            var Q2;
            Q2=makeQuery(id+"F2.opExtrude","CAP_FACE",FACE,{"disambiguationData":[OSD([sQuery(id+"F0.wireOp",EDGE,"E0"),sQuery(id+"F0.wireOp",EDGE,"E1"),sQuery(id+"F0.wireOp",EDGE,"E4"),sQuery(id+"F0.wireOp",EDGE,"E5"),sQuery(id+"F0.wireOp",EDGE,"E6"),sQuery(id+"F0.wireOp",EDGE,"E7"),sQuery(id+"F0.wireOp",EDGE,"E8"),sQuery(id+"F0.wireOp",EDGE,"E9"),sQuery(id+"F0.wireOp",EDGE,"E12"),sQuery(id+"F0.wireOp",EDGE,"E13"),sQuery(id+"F0.wireOp",EDGE,"E16"),sQuery(id+"F0.wireOp",EDGE,"E17"),sQuery(id+"F0.wireOp",EDGE,"E20"),sQuery(id+"F0.wireOp",EDGE,"E22"),sQuery(id+"F0.wireOp",EDGE,"E23"),sQuery(id+"F0.wireOp",EDGE,"E26"),sQuery(id+"F0.wireOp",EDGE,"E24"),sQuery(id+"F0.wireOp",EDGE,"E27"),sQuery(id+"F0.wireOp",EDGE,"E28"),sQuery(id+"F0.wireOp",EDGE,"E39"),sQuery(id+"F0.wireOp",EDGE,"E40"),sQuery(id+"F0.wireOp",EDGE,"E42"),sQuery(id+"F0.wireOp",EDGE,"E43"),sQuery(id+"F0.wireOp",EDGE,"E44"),sQuery(id+"F0.wireOp",EDGE,"E45"),sQuery(id+"F0.wireOp",EDGE,"E46"),sQuery(id+"F0.wireOp",EDGE,"E47"),sQuery(id+"F0.wireOp",EDGE,"E48"),sQuery(id+"F0.wireOp",EDGE,"E49"),sQuery(id+"F0.wireOp",EDGE,"E50"),sQuery(id+"F0.wireOp",EDGE,"E52"),sQuery(id+"F0.wireOp",EDGE,"E53"),sQuery(id+"F0.wireOp",EDGE,"E54"),sQuery(id+"F0.wireOp",EDGE,"E55"),sQuery(id+"F0.wireOp",EDGE,"E56"),sQuery(id+"F0.wireOp",EDGE,"E57"),sQuery(id+"F0.wireOp",EDGE,"E59"),sQuery(id+"F0.wireOp",EDGE,"E60"),sQuery(id+"F0.wireOp",EDGE,"E61"),sQuery(id+"F0.wireOp",EDGE,"E63"),sQuery(id+"F0.wireOp",EDGE,"E64"),sQuery(id+"F0.wireOp",EDGE,"E65"),sQuery(id+"F0.wireOp",EDGE,"E66"),sQuery(id+"F0.wireOp",EDGE,"E104")])],"isStart":false});
            var Q3;
            Q3=makeQuery(id+"F2.opExtrude","CAP_FACE",FACE,{"disambiguationData":[OSD([sQuery(id+"F1.wireOp",EDGE,"E117")])],"isStart":false});
            var Q4;
            Q4=makeQuery(id+"F2.opExtrude","CAP_FACE",FACE,{"disambiguationData":[OSD([sQuery(id+"F1.wireOp",EDGE,"E117")])],"isStart":true});
            var Q5;
            Q5=makeQuery(id+"F2.opExtrude","CAP_FACE",FACE,{"disambiguationData":[OSD([sQuery(id+"F1.wireOp",EDGE,"E116")])],"isStart":false});
            var Q6;
            Q6=makeQuery(id+"F2.opExtrude","CAP_FACE",FACE,{"disambiguationData":[OSD([sQuery(id+"F1.wireOp",EDGE,"E116")])],"isStart":true});
            extrude(context, id + "F5", {"entities" : qUnion([Q0, Q1, Q2, Q3, Q4, Q5, Q6]), "oppositeDirection" : true, "depth" : 3 * mm, "offsetDistance" : 25 * mm});
        }
    });
